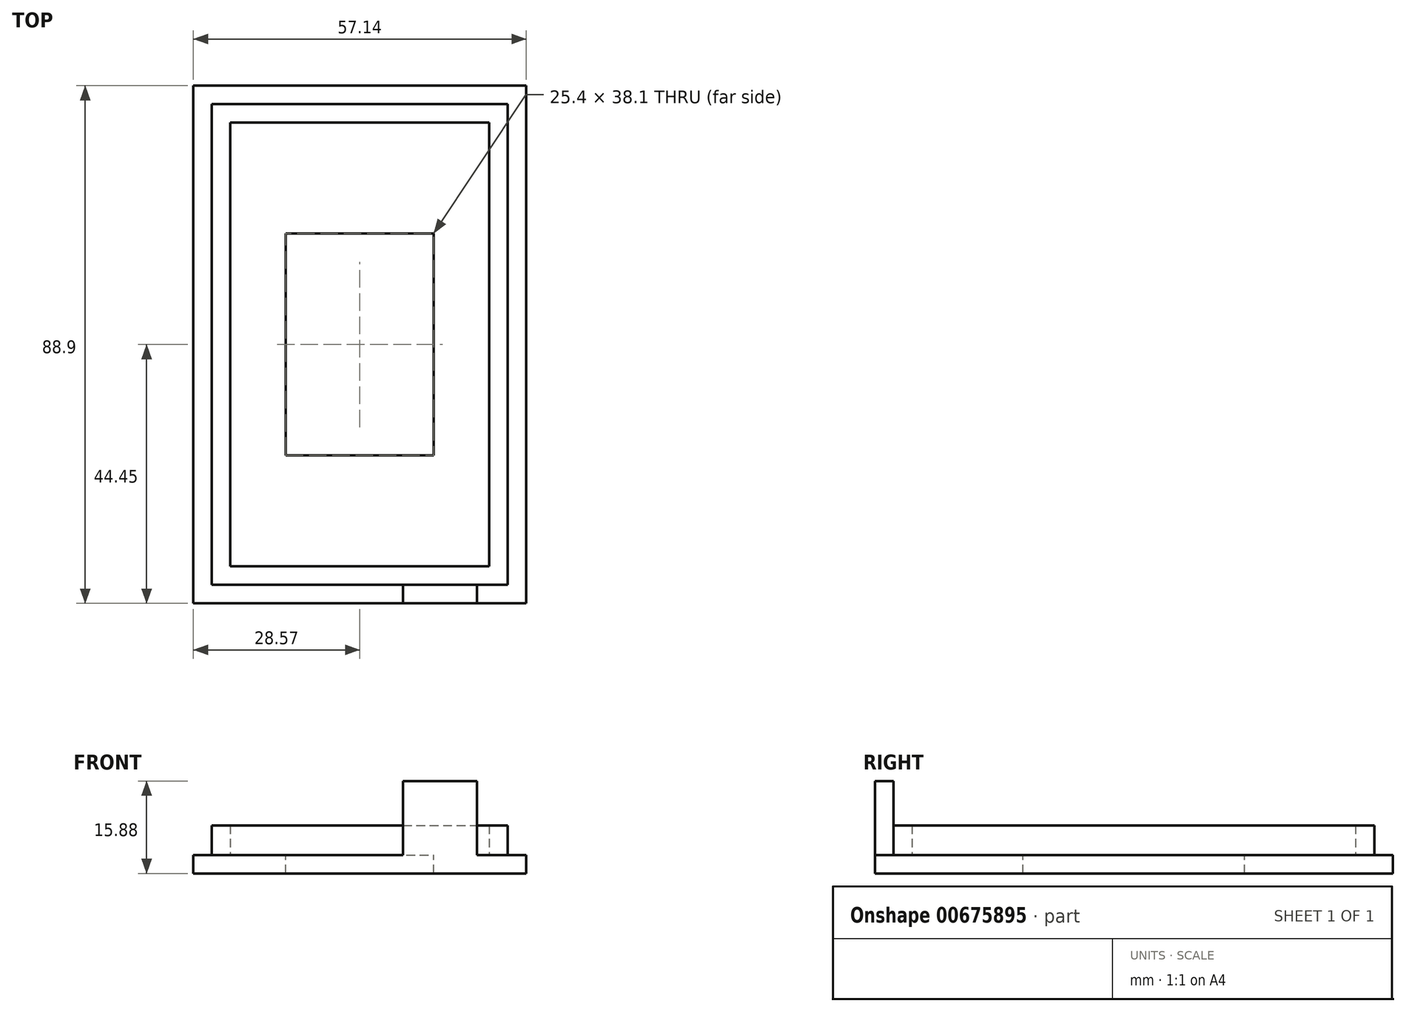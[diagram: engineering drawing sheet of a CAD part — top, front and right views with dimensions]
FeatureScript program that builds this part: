
annotation { "Feature Type Name" : "Feature", "Feature Type Description" : "" }
export const myFeature = defineFeature(function(context is Context, id is Id, definition is map)
    precondition{}
    {
        {
            var Q0;
            Q0=qCreatedBy(makeId("Top.planeOp"),FACE);
            var sketch = newSketch(context, id + "F0", { "sketchPlane" : qUnion([Q0])});
            skLineSegment(sketch, "E0.bottom", {"start": v(-28.57, 44.45) * mm, "end": v(28.58, 44.45) * mm});
            skLineSegment(sketch, "E0.top", {"start": v(-28.58, -44.45) * mm, "end": v(28.57, -44.45) * mm});
            skLineSegment(sketch, "E0.left", {"start": v(-28.57, 44.45) * mm, "end": v(-28.58, -44.45) * mm});
            skLineSegment(sketch, "E0.right", {"start": v(28.58, 44.45) * mm, "end": v(28.57, -44.45) * mm});
            skPoint(sketch, "E0.middle", {"position": v(0, 0) * mm});
            skSolve(sketch);
        }
        {
            var Q0;
            Q0=makeQuery(id+"F0.imprint","IMPRINT",FACE,{"disambiguationData":[TD([[makeQuery(id+"F0.imprint","IMPRINT",EDGE,{"derivedFrom":sQuery(id+"F0.wireOp",EDGE,"E0.bottom")}),-1.0]])]});
            extrude(context, id + "F1", {"entities" : qUnion([Q0]), "depth" : 3.17 * mm, "offsetDistance" : 25.4 * mm});
        }
        {
            var Q0;
            Q0=makeQuery(id+"F1.opExtrude","CAP_FACE",FACE,{"disambiguationData":[OSD([sQuery(id+"F0.wireOp",EDGE,"E0.bottom"),sQuery(id+"F0.wireOp",EDGE,"E0.top"),sQuery(id+"F0.wireOp",EDGE,"E0.left"),sQuery(id+"F0.wireOp",EDGE,"E0.right")])],"isStart":false});
            var sketch = newSketch(context, id + "F2", { "sketchPlane" : qUnion([Q0])});
            skLineSegment(sketch, "E1.bottom", {"start": v(-25.4, 41.28) * mm, "end": v(25.4, 41.28) * mm});
            skLineSegment(sketch, "E1.top", {"start": v(-25.4, -41.28) * mm, "end": v(25.4, -41.28) * mm});
            skLineSegment(sketch, "E1.left", {"start": v(-25.4, 41.28) * mm, "end": v(-25.4, -41.28) * mm});
            skLineSegment(sketch, "E1.right", {"start": v(25.4, 41.28) * mm, "end": v(25.4, -41.28) * mm});
            skPoint(sketch, "E1.middle", {"position": v(0, 0) * mm});
            skSolve(sketch);
        }
        {
            var Q0;
            Q0=makeQuery(id+"F2.imprint","IMPRINT",FACE,{"disambiguationData":[TD([[makeQuery(id+"F2.imprint","IMPRINT",EDGE,{"derivedFrom":sQuery(id+"F2.wireOp",EDGE,"E1.bottom")}),-1.0]])]});
            extrude(context, id + "F3", {"entities" : qUnion([Q0]), "operationType" : NewBodyOperationType.ADD, "depth" : 5.08 * mm, "offsetDistance" : 25.4 * mm});
        }
        {
            var Q0;
            Q0=makeQuery(id+"F3.opExtrude","CAP_FACE",FACE,{"disambiguationData":[OSD([sQuery(id+"F2.wireOp",EDGE,"E1.bottom"),sQuery(id+"F2.wireOp",EDGE,"E1.top"),sQuery(id+"F2.wireOp",EDGE,"E1.left"),sQuery(id+"F2.wireOp",EDGE,"E1.right")])],"isStart":false});
            shell(context, id + "F4", {"entities" : qUnion([Q0]), "thickness" : 3.17 * mm});
        }
        {
            var Q0;
            Q0=makeQuery(id+"F4.opShell","OFFSET_FACE",FACE,{"disambiguationData":[OSD([sQuery(id+"F0.wireOp",EDGE,"E0.bottom"),sQuery(id+"F0.wireOp",EDGE,"E0.top"),sQuery(id+"F0.wireOp",EDGE,"E0.left"),sQuery(id+"F0.wireOp",EDGE,"E0.right")])]});
            var sketch = newSketch(context, id + "F5", { "sketchPlane" : qUnion([Q0])});
            skLineSegment(sketch, "E2.bottom", {"start": v(-12.7, 19.05) * mm, "end": v(12.7, 19.05) * mm});
            skLineSegment(sketch, "E2.top", {"start": v(-12.7, -19.05) * mm, "end": v(12.7, -19.05) * mm});
            skLineSegment(sketch, "E2.left", {"start": v(-12.7, 19.05) * mm, "end": v(-12.7, -19.05) * mm});
            skLineSegment(sketch, "E2.right", {"start": v(12.7, 19.05) * mm, "end": v(12.7, -19.05) * mm});
            skPoint(sketch, "E2.middle", {"position": v(0, 0) * mm});
            skSolve(sketch);
        }
        {
            var Q0;
            Q0=makeQuery(id+"F5.imprint","IMPRINT",FACE,{"disambiguationData":[TD([[makeQuery(id+"F5.imprint","IMPRINT",EDGE,{"derivedFrom":sQuery(id+"F5.wireOp",EDGE,"E2.bottom")}),-1.0]])]});
            extrude(context, id + "F6", {"entities" : qUnion([Q0]), "operationType" : NewBodyOperationType.REMOVE, "oppositeDirection" : true, "depth" : 25.4 * mm, "offsetDistance" : 25.4 * mm});
        }
        {
            var Q0;
            Q0=makeQuery(id+"F3.opExtrude","SWEPT_FACE",FACE,{"disambiguationData":[OSD([sQuery(id+"F2.wireOp",EDGE,"E1.top")])]});
            var sketch = newSketch(context, id + "F7", { "sketchPlane" : qUnion([Q0])});
            skLineSegment(sketch, "E3.bottom", {"start": v(7.42, 3.18) * mm, "end": v(20.12, 3.18) * mm});
            skLineSegment(sketch, "E3.top", {"start": v(7.42, 15.88) * mm, "end": v(20.12, 15.88) * mm});
            skLineSegment(sketch, "E3.left", {"start": v(7.42, 3.18) * mm, "end": v(7.42, 15.88) * mm});
            skLineSegment(sketch, "E3.right", {"start": v(20.12, 3.18) * mm, "end": v(20.12, 15.88) * mm});
            skLineSegment(sketch, "E4", {"start": v(-25.4, 8.26) * mm, "end": v(-20.65, 8.26) * mm});
            skLineSegment(sketch, "E5", {"start": v(25.4, 8.26) * mm, "end": v(20.65, 8.26) * mm});
            skSolve(sketch);
        }
        {
            var Q0;
            {var subQ0=sQuery(id+"F7.wireOp",EDGE,"E3.top");Q0=makeQuery(id+"F7.imprint","IMPRINT",FACE,{"disambiguationData":[TD([[makeQuery(id+"F7.imprint","IMPRINT",EDGE,{"derivedFrom":subQ0}),-1.0]])]});}
            var Q1;
            {var subQ0=sQuery(id+"F7.wireOp",EDGE,"E3.bottom");Q1=makeQuery(id+"F7.imprint","IMPRINT",FACE,{"disambiguationData":[TD([[makeQuery(id+"F7.imprint","IMPRINT",EDGE,{"derivedFrom":subQ0}),1.0]])]});}
            extrude(context, id + "F8", {"entities" : qUnion([Q0, Q1]), "operationType" : NewBodyOperationType.ADD, "depth" : 3.17 * mm, "offsetDistance" : 25.4 * mm});
        }
    });
